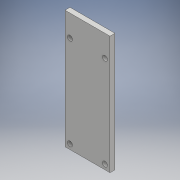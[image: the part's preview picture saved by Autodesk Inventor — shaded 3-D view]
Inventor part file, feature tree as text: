
AUTODESK INVENTOR PART (.ipt)
format: ipt  version: 2017 (Build 210142000, 142)  size: 107,520 bytes
history: native  units: mm
features: extrude x2, sketch x2
ambient origin geometry x8: Origin, YZ Plane, XZ Plane, XY Plane, X Axis, Y Axis, Z Axis, Center Point
bodies: Solid1 (feature_tree)
feature tree (4):
  extrude  "Extrusion1"  Depth=27.0mm
  extrude  "Extrusion2"  Depth=3.0mm
  sketch  "Sketch1"  dims[d0=71.0mm d1=27.0mm]
  sketch  "Sketch2"  dims[d2=3.0mm d3=0.0mm d4=3.0mm d5=3.0mm d6=13.0mm d7=20.0mm d9=55.0mm d10=20.0mm d12=21.0mm d15=3.0mm d16=0.0mm]
